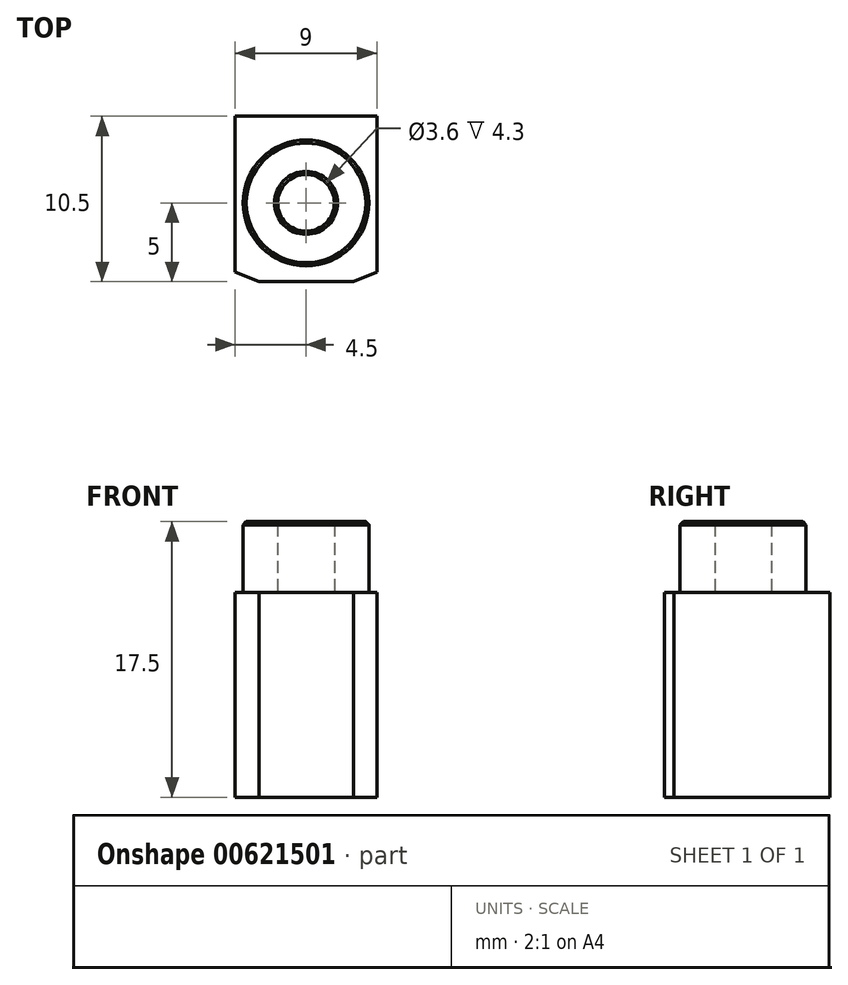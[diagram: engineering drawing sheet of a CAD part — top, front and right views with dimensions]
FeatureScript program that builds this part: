
annotation { "Feature Type Name" : "Feature", "Feature Type Description" : "" }
export const myFeature = defineFeature(function(context is Context, id is Id, definition is map)
    precondition{}
    {
        {
            var Q0;
            Q0=qCreatedBy(makeId("Top.planeOp"),FACE);
            var sketch = newSketch(context, id + "F0", { "sketchPlane" : qUnion([Q0])});
            skLineSegment(sketch, "E0", {"start": v(0, 5.5) * mm, "end": v(-4.5, 5.5) * mm});
            skLineSegment(sketch, "E1", {"start": v(-4.5, 5.5) * mm, "end": v(-4.5, -4.4) * mm});
            skLineSegment(sketch, "E2", {"start": v(-4.5, -4.4) * mm, "end": v(-3, -5) * mm});
            skLineSegment(sketch, "E3", {"start": v(-3, -5) * mm, "end": v(0, -5) * mm});
            skLineSegment(sketch, "E4", {"start": v(0, 8.68) * mm, "end": v(0, -9.4) * mm, "construction": true});
            skLineSegment(sketch, "E5.MirrorCS", {"start": v(4.5, 5.5) * mm, "end": v(4.5, -4.4) * mm});
            skLineSegment(sketch, "E6.MirrorCS", {"start": v(0, 5.5) * mm, "end": v(4.5, 5.5) * mm});
            skLineSegment(sketch, "E7.MirrorCS", {"start": v(4.5, -4.4) * mm, "end": v(3, -5) * mm});
            skLineSegment(sketch, "E8.MirrorCS", {"start": v(3, -5) * mm, "end": v(0, -5) * mm});
            skSolve(sketch);
        }
        {
            var Q0;
            Q0 = qSketchRegion(id + "F0", true);
            extrude(context, id + "F1", {"entities" : qUnion([Q0]), "depth" : 13 * mm, "offsetDistance" : 25 * mm});
        }
        {
            var Q0;
            Q0=makeQuery(id+"F1.opExtrude","CAP_FACE",FACE,{"disambiguationData":[OSD([sQuery(id+"F0.wireOp",EDGE,"E0"),sQuery(id+"F0.wireOp",EDGE,"E1"),sQuery(id+"F0.wireOp",EDGE,"E2"),sQuery(id+"F0.wireOp",EDGE,"E3"),sQuery(id+"F0.wireOp",EDGE,"E5.MirrorCS"),sQuery(id+"F0.wireOp",EDGE,"E6.MirrorCS"),sQuery(id+"F0.wireOp",EDGE,"E7.MirrorCS"),sQuery(id+"F0.wireOp",EDGE,"E8.MirrorCS")])],"isStart":false});
            var sketch = newSketch(context, id + "F2", { "sketchPlane" : qUnion([Q0])});
            skPoint(sketch, "E9.0", {"position": v(0, 0) * mm});
            skCircle(sketch, "E10", {"center": v(0, 0) * mm, "radius": 4 * mm});
            skCircle(sketch, "E11", {"center": v(0, 0) * mm, "radius": 1.8 * mm});
            skSolve(sketch);
        }
        {
            var Q0;
            Q0 = qSketchRegion(id + "F2", true);
            extrude(context, id + "F3", {"entities" : qUnion([Q0]), "operationType" : NewBodyOperationType.ADD, "depth" : 4.5 * mm, "offsetDistance" : 25 * mm});
        }
        {
            var Q0;
            Q0=makeQuery(id+"F3.opExtrude","CAP_EDGE",EDGE,{"disambiguationData":[OSD([sQuery(id+"F2.wireOp",EDGE,"E10")])],"isStart":false});
            var Q1;
            Q1=makeQuery(id+"F3.opExtrude","CAP_EDGE",EDGE,{"disambiguationData":[OSD([sQuery(id+"F2.wireOp",EDGE,"E11")])],"isStart":false});
            chamfer(context, id + "F4", {"entities" : qUnion([Q0, Q1]), "width" : .2 * mm, "tangentPropagation" : true});
        }
    });
